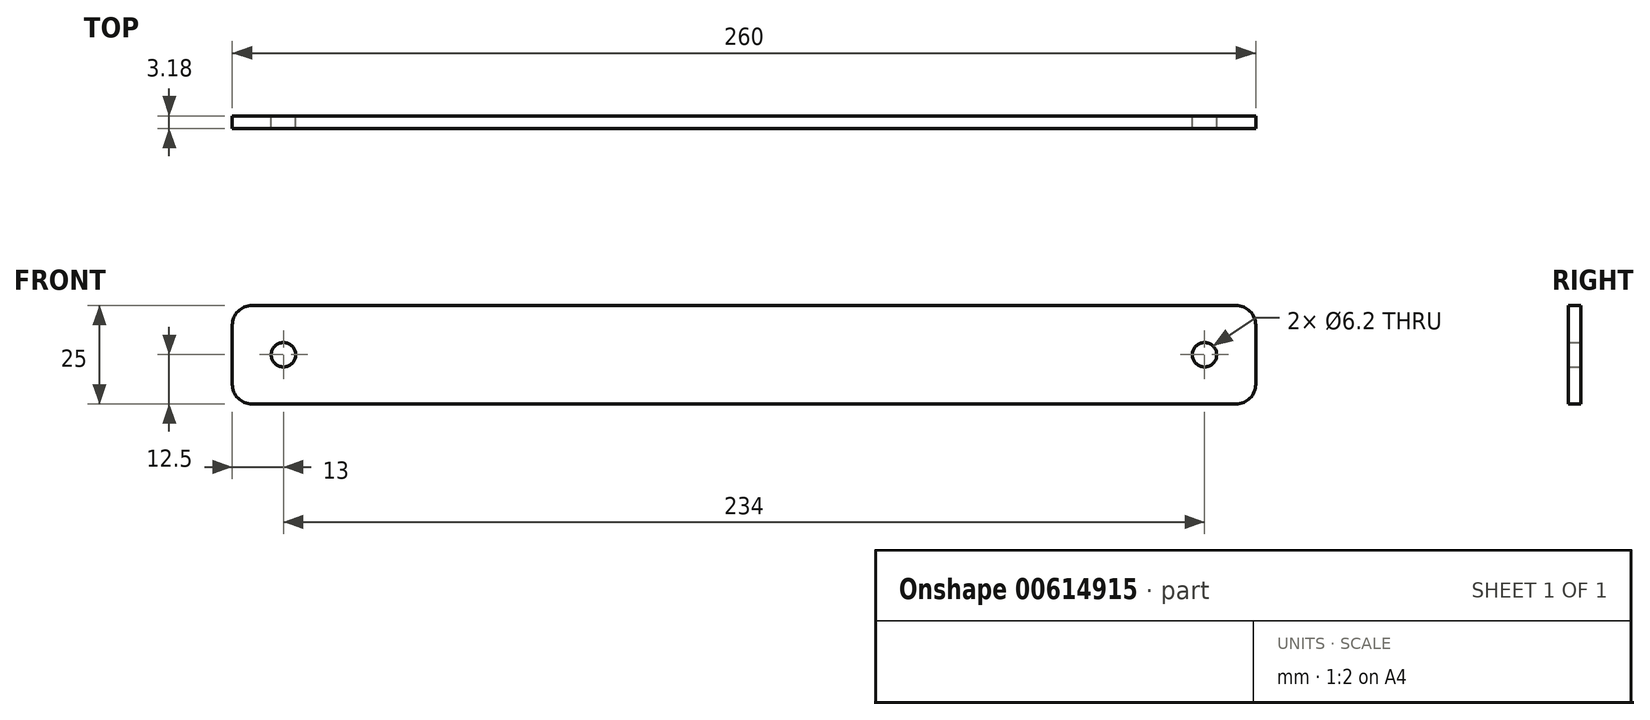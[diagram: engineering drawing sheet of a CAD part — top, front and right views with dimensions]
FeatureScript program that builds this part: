
annotation { "Feature Type Name" : "Feature", "Feature Type Description" : "" }
export const myFeature = defineFeature(function(context is Context, id is Id, definition is map)
    precondition{}
    {
        {
            var Q0;
            Q0=qCreatedBy(makeId("Front.planeOp"),FACE);
            var sketch = newSketch(context, id + "F0", { "sketchPlane" : qUnion([Q0])});
            skLineSegment(sketch, "E0.bottom", {"start": v(-125, 12.5) * mm, "end": v(125, 12.5) * mm});
            skLineSegment(sketch, "E0.top", {"start": v(-125, -12.5) * mm, "end": v(125, -12.5) * mm});
            skLineSegment(sketch, "E0.left", {"start": v(-130, 7.5) * mm, "end": v(-130, -7.5) * mm});
            skLineSegment(sketch, "E0.right", {"start": v(130, 7.5) * mm, "end": v(130, -7.5) * mm});
            skPoint(sketch, "E0.middle", {"position": v(0, 0) * mm});
            skLineSegment(sketch, "E1", {"start": v(0, 0) * mm, "end": v(117, 0) * mm});
            skCircle(sketch, "E2", {"center": v(117, 0) * mm, "radius": 3.1 * mm});
            skLineSegment(sketch, "E3", {"start": v(0, 0) * mm, "end": v(-117, 0) * mm});
            skCircle(sketch, "E4", {"center": v(-117, 0) * mm, "radius": 3.1 * mm});
            skPoint(sketch, "E5.visualSharp", {"position": v(130, 12.5) * mm});
            skArc(sketch, "E5.filletArc", {"start": v(130, 7.5) * mm, "mid": v(128.54, 11.04) * mm, "end": v(125, 12.5) * mm});
            skPoint(sketch, "E6.visualSharp", {"position": v(130, -12.5) * mm});
            skArc(sketch, "E6.filletArc", {"start": v(125, -12.5) * mm, "mid": v(128.54, -11.04) * mm, "end": v(130, -7.5) * mm});
            skPoint(sketch, "E7.visualSharp", {"position": v(-130, 12.5) * mm});
            skArc(sketch, "E7.filletArc", {"start": v(-125, 12.5) * mm, "mid": v(-128.54, 11.04) * mm, "end": v(-130, 7.5) * mm});
            skPoint(sketch, "E8.visualSharp", {"position": v(-130, -12.5) * mm});
            skArc(sketch, "E8.filletArc", {"start": v(-130, -7.5) * mm, "mid": v(-128.54, -11.04) * mm, "end": v(-125, -12.5) * mm});
            skSolve(sketch);
        }
        {
            var Q0;
            Q0=makeQuery(id+"F0.imprint","IMPRINT",FACE,{"disambiguationData":[TD([[makeQuery(id+"F0.imprint","IMPRINT",EDGE,{"derivedFrom":sQuery(id+"F0.wireOp",EDGE,"E0.bottom")}),-1.0]])]});
            extrude(context, id + "F1", {"entities" : qUnion([Q0]), "depth" : 3.17 * mm, "offsetDistance" : 25 * mm});
        }
    });
